# Revit family: OL2-HTSALRLG1CMWMM-EXIT SIGN
name_source: partatom
category: Lighting Fixtures
units: mm (PartAtom-declared; Revit-internal decimal feet)

## family parameters
Cut with Voids When Loaded = No
Host = Face
Light Source = No
Maintain Annotation Orientation = No
Part Type = Normal
Room Calculation Point = No
Round Connector Dimension = Use Diameter
Shared = No

## types (6) — shared parameters
BOTTOM MATERIAL = BOTTOM MATERIAL BLACK
Default Elevation = 1219 mm
HOUSING MATERIAL = HOUSING MATERIAL
Lamp = LED
Manufacturer = BEGHELLI
Model = OL2HTSALRLG1CMWMM
Type Image = OL2 MULLION MOUNTED IMAGE.jpg
Wattage Comments = 2W

## per-type parameters (varying)
| type | FACE MATERIAL | LETTER MATERIAL |
| OL2HTLR1CMM | FACE MATERIAL CLEAR | LETTER MATERIAL RED |
| OL2HTLG1CMM | FACE MATERIAL CLEAR | LETTER MATERIAL GREEN |
| OL2HTLR1MMM | FACE MATERIAL MIRROR | LETTER MATERIAL RED |
| OL2HTLG1MMM | FACE MATERIAL MIRROR | LETTER MATERIAL GREEN |
| OL2HTLR1WMM | FACE MATERIAL WHITE | LETTER MATERIAL RED |
| OL2HTLG1WMM | FACE MATERIAL WHITE | LETTER MATERIAL GREEN |

## geometry (parser evidence)
native form markers: Sweep x9
no freeform markers — native parametric forms only
